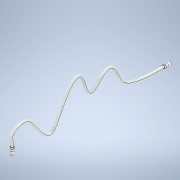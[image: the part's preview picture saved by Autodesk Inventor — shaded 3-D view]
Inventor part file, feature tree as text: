
AUTODESK INVENTOR PART (.ipt)
format: ipt  version: 2020 (Build 240168000, 168)  size: 696,832 bytes
history: native  units: mm
features: other x8, sketch x4, revolve x2, sweep x1, plane x1
ambient origin geometry x8: Origin, YZ Plane, XZ Plane, XY Plane, X Axis, Y Axis, Z Axis, Center Point
bodies: Solid1 (feature_tree)
feature tree (16):
  revolve  "Revolution1"  [1 undecoded]
  sweep  "Sweep1"
  other  "UCS1"
  plane  "Work Plane3"
  revolve  "Revolution3"  [1 undecoded]
  sketch  "Sketch2"  dims[d0=25.0mm d2=12.75mm]
  sketch  "Sketch3"  dims[d4=13.75mm d5=0.75mm]
  sketch  "Sketch4"  dims[d6=90.0deg d7=1.0mm]
  sketch  "Sketch7"  dims[d8=10.0mm d10=29.0mm d11=11.0mm d12=8.0mm d13=90.0deg d14=18.0mm d15=21.0mm d16=0.0mm d17=0.0mm d33=0.0mm d34=0.0mm d35=0.0mm d36=0.0mm d37=0.0mm d38=0.0mm d39=25.0mm d40=12.75mm d41=45.0mm d42=0.75mm d43=90.0deg d44=1.0mm d45=10.0mm d46=29.0mm d47=11.0mm d48=8.0mm d49=8.0mm d50=9.0mm d51=90.0deg]
  other  "UCS1: YZ Plane"
  other  "UCS1: XZ Plane"
  other  "UCS1: XY Plane"
  other  "UCS1: X Axis"
  other  "UCS1: Y Axis"
  other  "UCS1: Z Axis"
  other  "UCS1: Center Point"
note: 2 required parameter values undecoded (feature->parameter linkage not recoverable at this tier; creation-order binding heuristic only, values carry confidence <= 0.55)
